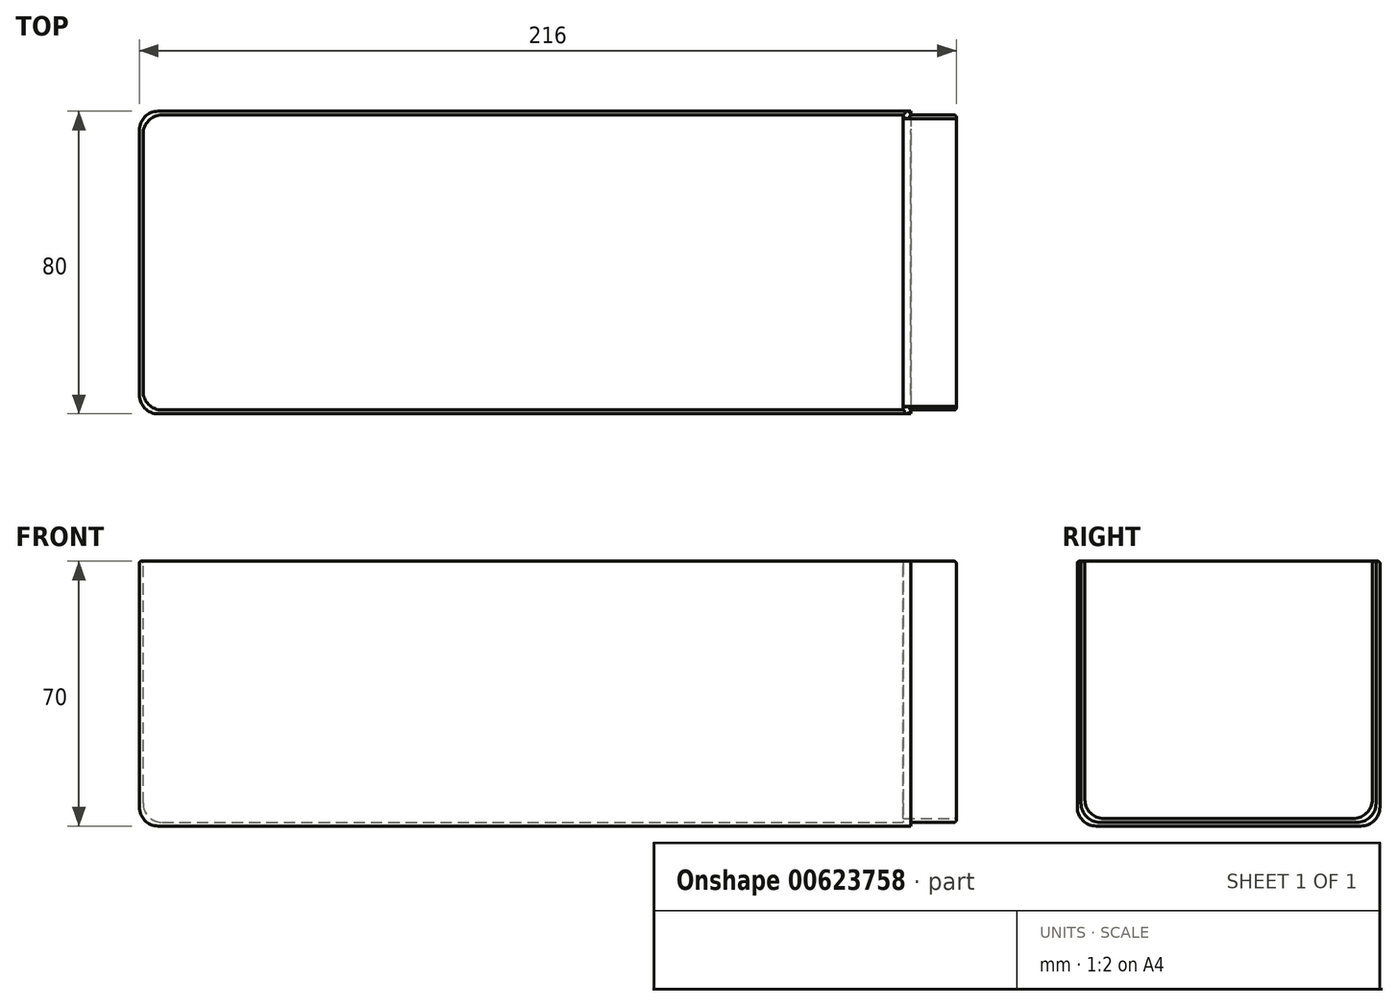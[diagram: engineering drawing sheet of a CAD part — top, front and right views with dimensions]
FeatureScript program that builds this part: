
annotation { "Feature Type Name" : "Feature", "Feature Type Description" : "" }
export const myFeature = defineFeature(function(context is Context, id is Id, definition is map)
    precondition{}
    {
        {
            var Q0;
            Q0=qCreatedBy(makeId("Top.planeOp"),FACE);
            var sketch = newSketch(context, id + "F0", { "sketchPlane" : qUnion([Q0])});
            skLineSegment(sketch, "E0.bottom", {"start": v(102, -40) * mm, "end": v(-102, -40) * mm});
            skLineSegment(sketch, "E0.top", {"start": v(102, 40) * mm, "end": v(-102, 40) * mm});
            skLineSegment(sketch, "E0.left", {"start": v(102, -40) * mm, "end": v(102, 40) * mm});
            skLineSegment(sketch, "E0.right", {"start": v(-102, -40) * mm, "end": v(-102, 40) * mm});
            skPoint(sketch, "E0.middle", {"position": v(0, 0) * mm});
            skSolve(sketch);
        }
        {
            var Q0;
            Q0=makeQuery(id+"F0.imprint","IMPRINT",FACE,{"disambiguationData":[TD([[makeQuery(id+"F0.imprint","IMPRINT",EDGE,{"derivedFrom":sQuery(id+"F0.wireOp",EDGE,"E0.bottom")}),-1.0]])]});
            extrude(context, id + "F1", {"entities" : qUnion([Q0]), "depth" : 70 * mm, "offsetDistance" : 25 * mm});
        }
        {
            var Q0;
            Q0=makeQuery(id+"F1.opExtrude","CAP_FACE",FACE,{"disambiguationData":[OSD([sQuery(id+"F0.wireOp",EDGE,"E0.bottom"),sQuery(id+"F0.wireOp",EDGE,"E0.top"),sQuery(id+"F0.wireOp",EDGE,"E0.left"),sQuery(id+"F0.wireOp",EDGE,"E0.right")])],"isStart":false});
            var sketch = newSketch(context, id + "F2", { "sketchPlane" : qUnion([Q0])});
            skLineSegment(sketch, "E1.bottom", {"start": v(-101, 39) * mm, "end": v(100, 39) * mm});
            skLineSegment(sketch, "E1.top", {"start": v(-101, -39) * mm, "end": v(100, -39) * mm});
            skLineSegment(sketch, "E1.left", {"start": v(-101, 39) * mm, "end": v(-101, -39) * mm});
            skLineSegment(sketch, "E1.right", {"start": v(100, 39) * mm, "end": v(100, -39) * mm});
            skLineSegment(sketch, "E2", {"start": v(-102, 20.59) * mm, "end": v(-101, 20.59) * mm});
            skLineSegment(sketch, "E3", {"start": v(-70.41, 40) * mm, "end": v(-70.41, 39) * mm});
            skLineSegment(sketch, "E4", {"start": v(-57.73, -39) * mm, "end": v(-57.73, -40) * mm});
            skLineSegment(sketch, "E5", {"start": v(100, -8.44) * mm, "end": v(102, -8.44) * mm});
            skSolve(sketch);
        }
        {
            var Q0;
            {var subQ4=sQuery(id+"F2.wireOp",EDGE,"E1.left");var subQ6=sQuery(id+"F2.wireOp",EDGE,"E1.bottom");var subQ9=makeQuery(id+"F2.imprint","INTERSECT",VERTEX,{"derivedFrom":[subQ6,subQ4]});Q0=makeQuery(id+"F2.imprint","IMPRINT",FACE,{"disambiguationData":[TD([[makeQuery(id+"F2.imprint","IMPRINT",EDGE,{"disambiguationData":[TD([[subQ9,-1.0]])],"derivedFrom":subQ6}),-1.0]])]});}
            extrude(context, id + "F3", {"entities" : qUnion([Q0]), "operationType" : NewBodyOperationType.REMOVE, "oppositeDirection" : true, "depth" : 69 * mm, "offsetDistance" : 25 * mm});
        }
        {
            var Q0;
            Q0=makeQuery(id+"F1.opExtrude","SWEPT_FACE",FACE,{"disambiguationData":[OSD([sQuery(id+"F0.wireOp",EDGE,"E0.left")])]});
            var sketch = newSketch(context, id + "F4", { "sketchPlane" : qUnion([Q0])});
            skLineSegment(sketch, "E6.bottom", {"start": v(38, 70) * mm, "end": v(-38, 70) * mm});
            skLineSegment(sketch, "E6.top", {"start": v(38, 2) * mm, "end": v(-38, 2) * mm});
            skLineSegment(sketch, "E6.left", {"start": v(38, 70) * mm, "end": v(38, 2) * mm});
            skLineSegment(sketch, "E6.right", {"start": v(-38, 70) * mm, "end": v(-38, 2) * mm});
            skLineSegment(sketch, "E7", {"start": v(-40, 42.3) * mm, "end": v(-38, 42.3) * mm});
            skSolve(sketch);
        }
        {
            var Q0;
            {var subQ1=sQuery(id+"F4.wireOp",EDGE,"E6.bottom");Q0=makeQuery(id+"F4.imprint","IMPRINT",FACE,{"disambiguationData":[TD([[makeQuery(id+"F4.imprint","IMPRINT",EDGE,{"derivedFrom":subQ1}),-1.0]])]});}
            extrude(context, id + "F5", {"entities" : qUnion([Q0]), "operationType" : NewBodyOperationType.REMOVE, "oppositeDirection" : true, "depth" : 2 * mm, "offsetDistance" : 25 * mm});
        }
        {
            var Q0;
            Q0=makeQuery(id+"F3.boolean.opBoolean","COPY",FACE,{"derivedFrom":makeQuery(id+"F3.opExtrude","SWEPT_FACE",FACE,{"disambiguationData":[OSD([sQuery(id+"F2.wireOp",EDGE,"E1.right")])]})});
            var sketch = newSketch(context, id + "F6", { "sketchPlane" : qUnion([Q0])});
            skSolve(sketch);
        }
        {
            var Q0;
            {var subQ0=sQuery(id+"F2.wireOp",EDGE,"E1.right");Q0=makeQuery(id+"F6.imprint","IMPRINT",FACE,{"disambiguationData":[TD([[makeQuery(id+"F6.imprint","IMPRINT",EDGE,{"derivedFrom":makeQuery(id+"F3.boolean.opBoolean","COPY",EDGE,{"derivedFrom":makeQuery(id+"F3.opExtrude","CAP_EDGE",EDGE,{"disambiguationData":[OSD([subQ0])],"isStart":false})})}),1.0]])]});}
            extrude(context, id + "F7", {"entities" : qUnion([Q0]), "operationType" : NewBodyOperationType.ADD, "oppositeDirection" : true, "depth" : 14 * mm, "offsetDistance" : 25 * mm});
        }
        {
            var Q0;
            Q0=makeQuery(id+"F3.boolean.opBoolean","COPY",EDGE,{"derivedFrom":makeQuery(id+"F3.opExtrude","CAP_EDGE",EDGE,{"disambiguationData":[OSD([sQuery(id+"F2.wireOp",EDGE,"E1.bottom")])],"isStart":false})});
            var Q1;
            Q1=makeQuery(id+"F3.boolean.opBoolean","COPY",EDGE,{"derivedFrom":makeQuery(id+"F3.opExtrude","CAP_EDGE",EDGE,{"disambiguationData":[OSD([sQuery(id+"F2.wireOp",EDGE,"E1.left")])],"isStart":false})});
            var Q2;
            Q2=makeQuery(id+"F3.boolean.opBoolean","COPY",EDGE,{"derivedFrom":makeQuery(id+"F3.opExtrude","CAP_EDGE",EDGE,{"disambiguationData":[OSD([sQuery(id+"F2.wireOp",EDGE,"E1.top")])],"isStart":false})});
            var Q3;
            Q3=makeQuery(id+"F1.opExtrude","CAP_EDGE",EDGE,{"disambiguationData":[OSD([sQuery(id+"F0.wireOp",EDGE,"E0.top")])],"isStart":true});
            var Q4;
            Q4=makeQuery(id+"F1.opExtrude","CAP_EDGE",EDGE,{"disambiguationData":[OSD([sQuery(id+"F0.wireOp",EDGE,"E0.right")])],"isStart":true});
            var Q5;
            Q5=makeQuery(id+"F1.opExtrude","CAP_EDGE",EDGE,{"disambiguationData":[OSD([sQuery(id+"F0.wireOp",EDGE,"E0.bottom")])],"isStart":true});
            var Q6;
            Q6=makeQuery(id+"F1.opExtrude","SWEPT_EDGE",EDGE,{"disambiguationData":[OSD([sQuery(id+"F0.wireOp",EDGE,"E0.bottom"),sQuery(id+"F0.wireOp",EDGE,"E0.right")])]});
            var Q7;
            Q7=makeQuery(id+"F1.opExtrude","SWEPT_EDGE",EDGE,{"disambiguationData":[OSD([sQuery(id+"F0.wireOp",EDGE,"E0.top"),sQuery(id+"F0.wireOp",EDGE,"E0.right")])]});
            var Q8;
            Q8=makeQuery(id+"F3.boolean.opBoolean","COPY",EDGE,{"derivedFrom":makeQuery(id+"F3.opExtrude","SWEPT_EDGE",EDGE,{"disambiguationData":[OSD([sQuery(id+"F2.wireOp",EDGE,"E1.bottom"),sQuery(id+"F2.wireOp",EDGE,"E1.left")])]})});
            var Q9;
            Q9=makeQuery(id+"F3.boolean.opBoolean","COPY",EDGE,{"derivedFrom":makeQuery(id+"F3.opExtrude","SWEPT_EDGE",EDGE,{"disambiguationData":[OSD([sQuery(id+"F2.wireOp",EDGE,"E1.top"),sQuery(id+"F2.wireOp",EDGE,"E1.left")])]})});
            var Q10;
            {var subQ0=sQuery(id+"F2.wireOp",EDGE,"E1.right");var subQ1=sQuery(id+"F2.wireOp",EDGE,"E1.bottom");Q10=makeQuery(id+"F7.opExtrude","SWEPT_EDGE",EDGE,{"disambiguationData":[OSD([subQ1,subQ0]),TDD([makeQuery(id+"F6.imprint","INTERSECT",VERTEX,{"derivedFrom":[makeQuery(id+"F3.boolean.opBoolean","COPY",EDGE,{"derivedFrom":makeQuery(id+"F3.opExtrude","SWEPT_EDGE",EDGE,{"disambiguationData":[OSD([subQ1,subQ0])]})}),makeQuery(id+"F3.boolean.opBoolean","COPY",EDGE,{"derivedFrom":makeQuery(id+"F3.opExtrude","CAP_EDGE",EDGE,{"disambiguationData":[OSD([subQ0])],"isStart":false})})]})])]});}
            var Q11;
            {var subQ0=sQuery(id+"F2.wireOp",EDGE,"E1.right");var subQ1=sQuery(id+"F2.wireOp",EDGE,"E1.top");Q11=makeQuery(id+"F7.opExtrude","SWEPT_EDGE",EDGE,{"disambiguationData":[OSD([subQ1,subQ0]),TDD([makeQuery(id+"F6.imprint","INTERSECT",VERTEX,{"derivedFrom":[makeQuery(id+"F3.boolean.opBoolean","COPY",EDGE,{"derivedFrom":makeQuery(id+"F3.opExtrude","SWEPT_EDGE",EDGE,{"disambiguationData":[OSD([subQ1,subQ0])]})}),makeQuery(id+"F3.boolean.opBoolean","COPY",EDGE,{"derivedFrom":makeQuery(id+"F3.opExtrude","CAP_EDGE",EDGE,{"disambiguationData":[OSD([subQ0])],"isStart":false})})]})])]});}
            var Q12;
            {var subQ0=sQuery(id+"F4.wireOp",EDGE,"E6.right");var subQ1=sQuery(id+"F4.wireOp",EDGE,"E6.top");Q12=makeQuery(id+"F7.boolean.opBoolean","MERGE",EDGE,{"derivedFrom":[makeQuery(id+"F5.boolean.opBoolean","COPY",EDGE,{"derivedFrom":makeQuery(id+"F5.opExtrude","SWEPT_EDGE",EDGE,{"disambiguationData":[OSD([subQ1,subQ0])]})}),makeQuery(id+"F7.opExtrude","SWEPT_EDGE",EDGE,{"disambiguationData":[OSD([subQ1,subQ0])]})]});}
            var Q13;
            {var subQ0=sQuery(id+"F4.wireOp",EDGE,"E6.left");var subQ1=sQuery(id+"F4.wireOp",EDGE,"E6.top");Q13=makeQuery(id+"F7.boolean.opBoolean","MERGE",EDGE,{"derivedFrom":[makeQuery(id+"F5.boolean.opBoolean","COPY",EDGE,{"derivedFrom":makeQuery(id+"F5.opExtrude","SWEPT_EDGE",EDGE,{"disambiguationData":[OSD([subQ1,subQ0])]})}),makeQuery(id+"F7.opExtrude","SWEPT_EDGE",EDGE,{"disambiguationData":[OSD([subQ1,subQ0])]})]});}
            fillet(context, id + "F8", {"entities" : qUnion([Q0, Q1, Q2, Q3, Q4, Q5, Q6, Q7, Q8, Q9, Q10, Q11, Q12, Q13]), "radius" : 5 * mm, "tangentPropagation" : true, "allowEdgeOverflow" : false});
        }
        {
            var Q0;
            {var subQ0=makeQuery(id+"F1.opExtrude","CAP_FACE",FACE,{"disambiguationData":[OSD([sQuery(id+"F0.wireOp",EDGE,"E0.bottom"),sQuery(id+"F0.wireOp",EDGE,"E0.top"),sQuery(id+"F0.wireOp",EDGE,"E0.left"),sQuery(id+"F0.wireOp",EDGE,"E0.right")])],"isStart":false});var subQ1=sQuery(id+"F2.wireOp",EDGE,"E1.right");var subQ3=makeQuery(id+"F3.boolean.opBoolean","COPY",EDGE,{"derivedFrom":makeQuery(id+"F3.opExtrude","CAP_EDGE",EDGE,{"disambiguationData":[OSD([subQ1])],"isStart":true})});Q0=makeQuery(id+"F7.boolean.opBoolean","MERGE",FACE,{"derivedFrom":[subQ0,makeQuery(id+"F7.opExtrude","SWEPT_FACE",FACE,{"disambiguationData":[OSD([subQ1]),TDD([makeQuery(id+"F6.imprint","IMPRINT",EDGE,{"derivedFrom":makeQuery(id+"F5.boolean.opBoolean","SPLIT",EDGE,{"disambiguationData":[TD([makeQuery(id+"F3.boolean.opBoolean","COPY",FACE,{"derivedFrom":makeQuery(id+"F3.opExtrude","SWEPT_FACE",FACE,{"disambiguationData":[OSD([sQuery(id+"F2.wireOp",EDGE,"E1.bottom")])]})})])],"derivedFrom":subQ3})})])]}),makeQuery(id+"F7.opExtrude","SWEPT_FACE",FACE,{"disambiguationData":[OSD([subQ1]),TDD([makeQuery(id+"F6.imprint","IMPRINT",EDGE,{"derivedFrom":makeQuery(id+"F5.boolean.opBoolean","SPLIT",EDGE,{"disambiguationData":[TD([makeQuery(id+"F3.boolean.opBoolean","COPY",FACE,{"derivedFrom":makeQuery(id+"F3.opExtrude","SWEPT_FACE",FACE,{"disambiguationData":[OSD([sQuery(id+"F2.wireOp",EDGE,"E1.top")])]})})])],"derivedFrom":subQ3})})])]})]});}
            var Q1;
            Q1=makeQuery(id+"F7.opExtrude","CAP_FACE",FACE,{"disambiguationData":[OSD([sQuery(id+"F2.wireOp",EDGE,"E1.bottom"),sQuery(id+"F2.wireOp",EDGE,"E1.top"),sQuery(id+"F2.wireOp",EDGE,"E1.right"),sQuery(id+"F4.wireOp",EDGE,"E6.top"),sQuery(id+"F4.wireOp",EDGE,"E6.left"),sQuery(id+"F4.wireOp",EDGE,"E6.right")])],"isStart":false});
            fillet(context, id + "F9", {"entities" : qUnion([Q0, Q1]), "radius" : .5 * mm, "tangentPropagation" : true, "allowEdgeOverflow" : false});
        }
    });
